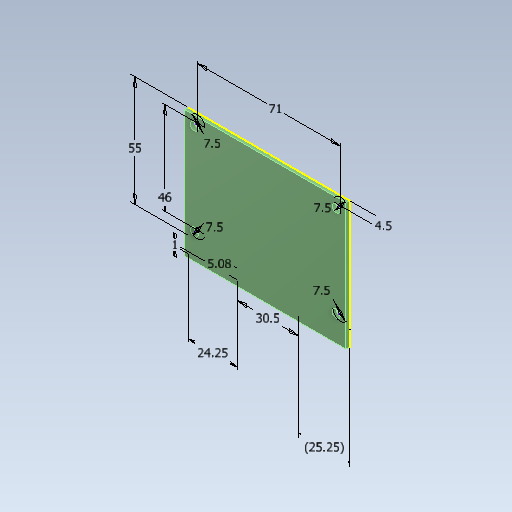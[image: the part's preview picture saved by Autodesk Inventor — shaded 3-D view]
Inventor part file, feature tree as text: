
AUTODESK INVENTOR PART (.ipt)
format: ipt  version: 2021 (Build 250183000, 183)  size: 133,632 bytes
history: native  units: mm
features: sketch x2, extrude x1, hole x1
ambient origin geometry x8: Origin, YZ Plane, XZ Plane, XY Plane, X Axis, Y Axis, Z Axis, Center Point
bodies: Solid1 (feature_tree)
feature tree (4):
  sketch  "Sketch1"  dims[d0=80.0mm d1=63.0mm]
  extrude  "Extrusion1"  Depth=63.0mm
  hole  "Hole1"  [1 undecoded]
  sketch  "Sketch2"  dims[d2=70.5mm d3=45.5mm d4=4.75mm d5=4.75mm d6=4.75mm d7=1.8mm d8=0.0mm d9=4.0mm d10=6.0mm d11=4.0mm d12=2.0mm d13=90.0deg d14=8.0mm d15=180.0deg d16=30.5mm d17=5.08mm d18=1.0mm d19=24.25mm d20=25.25mm d21=55.0mm d24=4.5mm d25=7.5mm d26=7.5mm d27=7.5mm d28=7.5mm d29=71.0mm d30=46.0mm]
note: 1 required parameter value undecoded (feature->parameter linkage not recoverable at this tier; creation-order binding heuristic only, values carry confidence <= 0.55)
